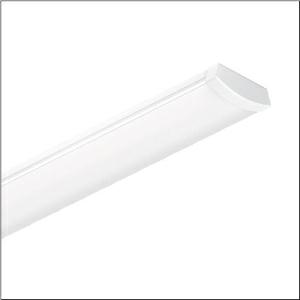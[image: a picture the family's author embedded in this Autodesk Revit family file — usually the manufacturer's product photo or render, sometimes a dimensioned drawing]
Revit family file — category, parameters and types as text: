
# Revit family: siluette_r__21_51ln12mdm20a_d267
name_source: partatom
category: Lighting Fixtures
units: mm (PartAtom-declared; Revit-internal decimal feet)

## family parameters
Cut with Voids When Loaded = No
Host = Face
Light Source = No
Part Type = Normal
Room Calculation Point = No
Round Connector Dimension = Use Diameter
Shared = No

## types (1)
- --- (1 x LED, 1510 lm, 12.2 W, 5000K)
    Apparent Load = 12 VA
    CIE Flux Codes = 43 73 92 94 100
    Color Rendering = 80
    Color Temperature = 5000K
    Default Elevation = 1800 mm
    Description = Siluette® 21, office luminaire, primary optical cover: enclosure, of PC, frosted, light emission: direct distribution, primary light characteristic: symmetric, installation type: suspended mounting, surface-mounted, LED, rated luminous flux: 2.600lm, luminous efficacy: 130lm/W, light colour: 830/840/850, colour temperature: 3000/4000/5000K, with terminal, 3-pole, mains connection: 220..240V, AC, 50/60Hz, rated input power: 20W, housing, of sheet steel, white, length: 600mm, width: 152mm, height: 53mm, end cap, of PMMA, white, protection rating (complete): IP44, insulation class (complete): insulation class I (protective earthing), certification: CE, UKCA, protection symbol: D, permissible operating ambient temperature: -20..+40°C, contact your sales advisor before using the luminaires in applications with unclear chemical exposure, large temperature fluctuations or condensation-forming humidity, corresponds to IFS (International Featured Standards) requirements for safety and quality in the food industry, packaging unit: 1 piece
    Height = 52 mm  [stored 0.170604 ft]
    Lamp = 1 x LED
    Lamp Light Flux = 1510 lm
    Lamp Power = 12.2 W
    Lamp count = 1
    Length = 645 mm
    Luminous efficacy = 124 lm/W
    Manufacturer = Siteco
    ModVariant = No
    Model = 51LN12MDM20A
    Mounting Place = Ceiling
    Mounting Type = Pendant
    Number of Poles = 1
    OnlyDefault = Yes
    Power Factor = 1
    Product Name = Siluette® 21
    Product group = office luminaire | ceiling pendant
    ProductGroupID = 902
    Protection Class = Protection class I
    Protection Degree = IP 44
    RLX_Detail_Level = 1
    RLX_Emergency_Light_Flux = 0 lm
    RLX_Emergency_Type = 0
    RLX_Emergency_Type_DB = No
    RlxData = <blob elided: 20157 chars, md5=949f4524>
    Socket = socket
    Standby Power = 0 W
    System Light Flux = 1510 lm
    System Power = 12 W
    Type Comments = individual setting: colour temperature 5000K, luminous flux: 57 % | (OFF | OFF | ON) | 200 mA
    Type Image = l_1296910.jpg
    URL = http://relux.com
    VarID = @adj_001883
    Voltage = 0 V
    Weight = 0.00 kg
    Width = 152 mm

note: [stored X ft] marks values corroborated as IEEE doubles in the binary element streams (Revit-internal decimal feet)

## geometry (parser evidence)
native form markers: Blend x4, Sweep x13
no freeform markers — native parametric forms only
